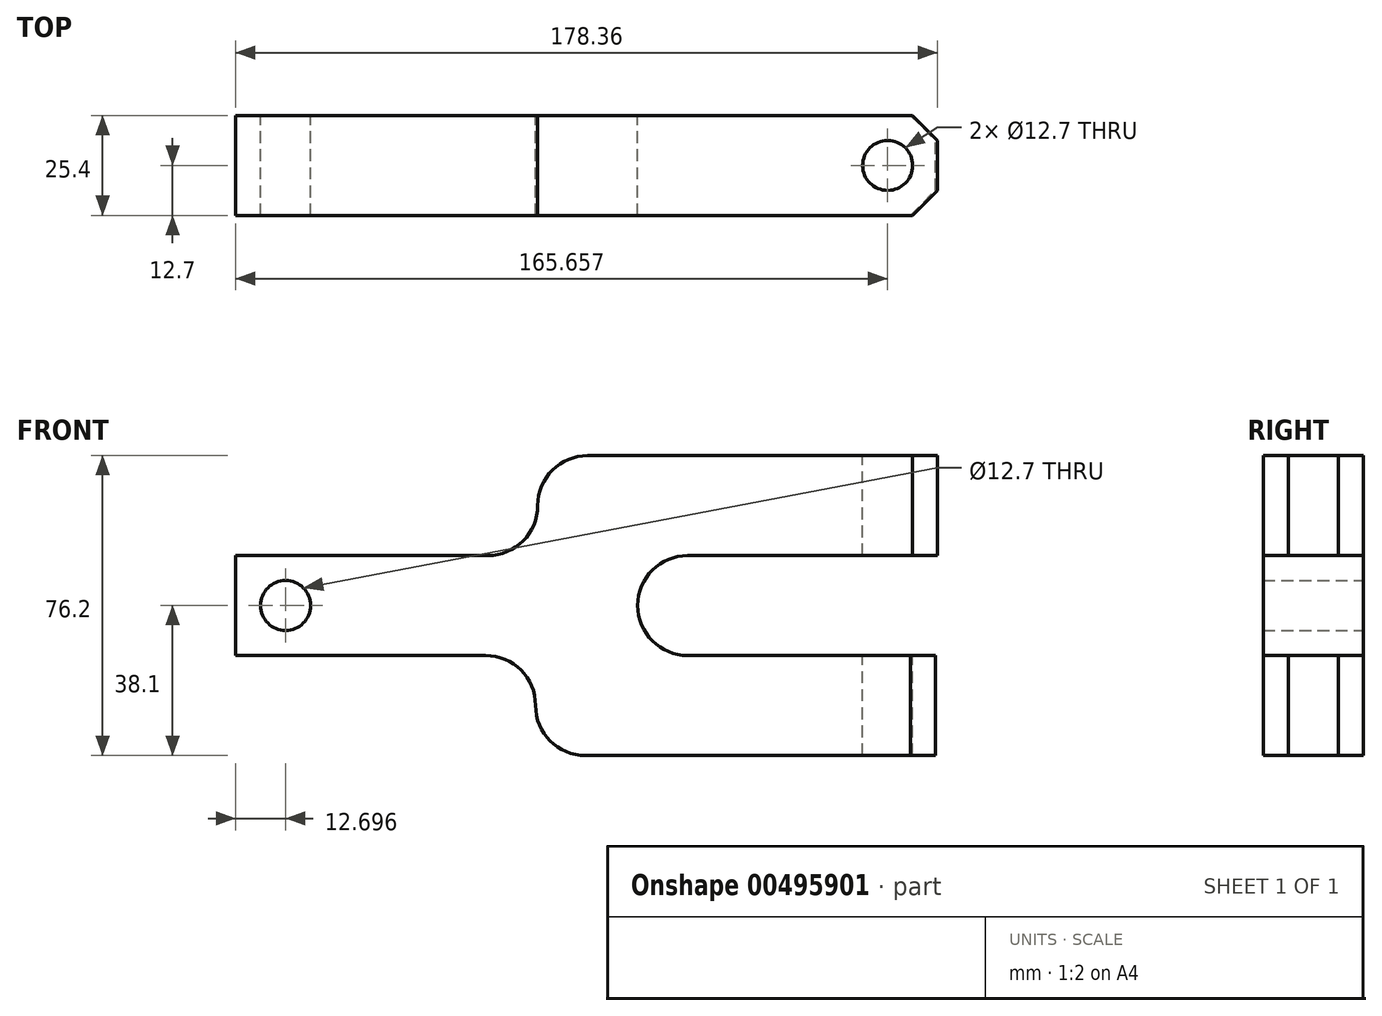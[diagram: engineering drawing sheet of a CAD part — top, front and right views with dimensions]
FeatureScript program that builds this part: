
annotation { "Feature Type Name" : "Feature", "Feature Type Description" : "" }
export const myFeature = defineFeature(function(context is Context, id is Id, definition is map)
    precondition{}
    {
        {
            var Q0;
            Q0=qCreatedBy(makeId("Front.planeOp"),FACE);
            var sketch = newSketch(context, id + "F0", { "sketchPlane" : qUnion([Q0])});
            skPoint(sketch, "E0.right.end.orphan", {"position": v(98.8, 49.55) * mm});
            skLineSegment(sketch, "E1.bottom", {"start": v(-86.46, 12.7) * mm, "end": v(-22.4, 12.7) * mm});
            skLineSegment(sketch, "E1.top", {"start": v(-86.46, -12.7) * mm, "end": v(-22.96, -12.7) * mm});
            skLineSegment(sketch, "E1.left", {"start": v(-86.46, 12.7) * mm, "end": v(-86.46, -12.7) * mm});
            skLineSegment(sketch, "E1.right", {"start": v(15.7, 0) * mm, "end": v(15.7, 0) * mm});
            skLineSegment(sketch, "E2.bottom", {"start": v(28.4, 12.7) * mm, "end": v(91.9, 12.7) * mm});
            skLineSegment(sketch, "E2.top", {"start": v(3, 38.1) * mm, "end": v(91.9, 38.1) * mm});
            skLineSegment(sketch, "E2.left", {"start": v(-9.7, 25.4) * mm, "end": v(-9.7, 25.4) * mm});
            skLineSegment(sketch, "E2.right", {"start": v(91.9, 12.7) * mm, "end": v(91.9, 38.1) * mm});
            skLineSegment(sketch, "E3.bottom", {"start": v(28.4, -12.7) * mm, "end": v(91.34, -12.7) * mm});
            skLineSegment(sketch, "E3.top", {"start": v(2.44, -38.1) * mm, "end": v(91.34, -38.1) * mm});
            skLineSegment(sketch, "E3.left", {"start": v(-10.26, -25.4) * mm, "end": v(-10.26, -25.4) * mm});
            skLineSegment(sketch, "E3.right", {"start": v(91.34, -12.7) * mm, "end": v(91.34, -38.1) * mm});
            skArc(sketch, "E4.filletArc", {"start": v(-22.4, 12.7) * mm, "mid": v(-13.42, 16.42) * mm, "end": v(-9.7, 25.4) * mm});
            skPoint(sketch, "E5.visualSharp", {"position": v(-9.7, 38.1) * mm});
            skArc(sketch, "E5.filletArc", {"start": v(3, 38.1) * mm, "mid": v(-5.98, 34.38) * mm, "end": v(-9.7, 25.4) * mm});
            skPoint(sketch, "E6.newPointB", {"position": v(15.7, 14.25) * mm});
            skArc(sketch, "E6.filletArc", {"start": v(28.4, 12.7) * mm, "mid": v(19.42, 8.98) * mm, "end": v(15.7, 0) * mm});
            skArc(sketch, "E7.filletArc", {"start": v(15.7, 0) * mm, "mid": v(19.42, -8.98) * mm, "end": v(28.4, -12.7) * mm});
            skPoint(sketch, "E8.newPointA", {"position": v(15.14, -12.7) * mm});
            skArc(sketch, "E8.filletArc", {"start": v(-10.26, -25.4) * mm, "mid": v(-13.98, -16.42) * mm, "end": v(-22.96, -12.7) * mm});
            skPoint(sketch, "E9.visualSharp", {"position": v(-10.26, -38.1) * mm});
            skArc(sketch, "E9.filletArc", {"start": v(-10.26, -25.4) * mm, "mid": v(-6.54, -34.38) * mm, "end": v(2.44, -38.1) * mm});
            skCircle(sketch, "E10", {"center": v(-73.76, 0) * mm, "radius": 6.35 * mm});
            skPoint(sketch, "E11", {"position": v(78.64, -38.1) * mm});
            skSolve(sketch);
        }
        {
            var Q0;
            Q0 = qSketchRegion(id + "F0", true);
            extrude(context, id + "F1", {"entities" : qUnion([Q0]), "depth" : 25.4 * mm});
        }
        {
            var Q0;
            Q0=qCreatedBy(makeId("Top.planeOp"),FACE);
            var sketch = newSketch(context, id + "F2", { "sketchPlane" : qUnion([Q0])});
            skCircle(sketch, "E12", {"center": v(79.2, -12.7) * mm, "radius": 6.35 * mm});
            skSolve(sketch);
        }
        {
            var Q0;
            Q0=makeQuery(id+"F2.imprint","IMPRINT",FACE,{"disambiguationData":[TD([[makeQuery(id+"F2.imprint","IMPRINT",EDGE,{"derivedFrom":sQuery(id+"F2.wireOp",EDGE,"E12")}),1.0]])]});
            var Q1;
            Q1=makeQuery(id+"F2.imprint","IMPRINT",EDGE,{"derivedFrom":sQuery(id+"F2.wireOp",EDGE,"E12")});
            extrude(context, id + "F3", {"entities" : qUnion([Q0]), "operationType" : NewBodyOperationType.REMOVE, "surfaceEntities" : qUnion([Q1]), "endBound" : BoundingType.SYMMETRIC, "oppositeDirection" : true, "depth" : 88.9 * mm});
        }
        {
            var Q0;
            Q0=makeQuery(id+"F1.opExtrude","CAP_EDGE",EDGE,{"disambiguationData":[OSD([sQuery(id+"F0.wireOp",EDGE,"E2.right")])],"isStart":true});
            var Q1;
            Q1=makeQuery(id+"F1.opExtrude","CAP_EDGE",EDGE,{"disambiguationData":[OSD([sQuery(id+"F0.wireOp",EDGE,"E3.right")])],"isStart":true});
            var Q2;
            Q2=makeQuery(id+"F1.opExtrude","CAP_EDGE",EDGE,{"disambiguationData":[OSD([sQuery(id+"F0.wireOp",EDGE,"E2.right")])],"isStart":false});
            var Q3;
            Q3=makeQuery(id+"F1.opExtrude","CAP_EDGE",EDGE,{"disambiguationData":[OSD([sQuery(id+"F0.wireOp",EDGE,"E3.right")])],"isStart":false});
            chamfer(context, id + "F4", {"entities" : qUnion([Q0, Q1, Q2, Q3]), "width" : 6.35 * mm, "tangentPropagation" : true});
        }
    });
